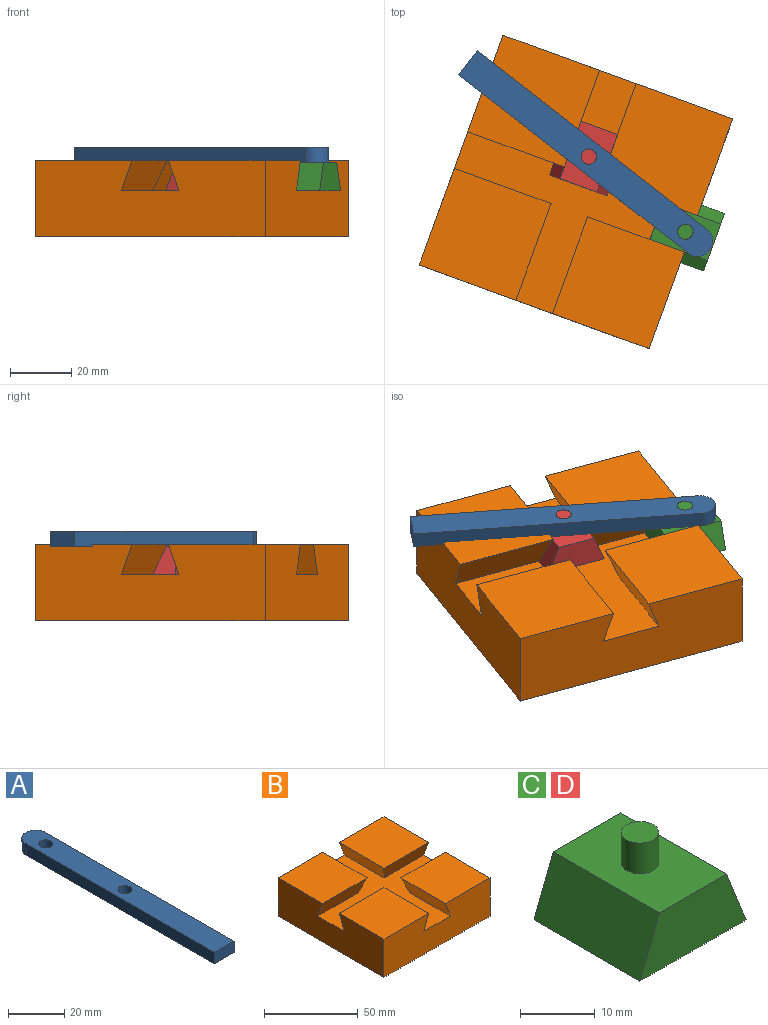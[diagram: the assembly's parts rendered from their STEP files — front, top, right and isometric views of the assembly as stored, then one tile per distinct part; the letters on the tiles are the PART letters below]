
ASSEMBLY  parts=4 mates=4
PART A: 8 faces, bbox 10x100x5 mm
  f0: plane 95x5mm, normal (-1,0,0), area 475mm2, adj f1,f5,f6,f7
  f1: plane 10x5mm, normal (0,-1,0), area 50mm2, adj f0,f2,f5,f6
  f2: plane 95x5mm, normal (1,0,0), area 475mm2, adj f1,f5,f6,f7
  f3: cylinder r=2.5mm len=5mm, axis (0,0,-1), area 78.5mm2, adj f5,f6
  f4: cylinder r=2.5mm len=5mm, axis (0,0,-1), area 78.5mm2, adj f5,f6
  f5: plane 100x10mm, normal (0,0,1), area 950mm2, adj f0,f1,f2,f3,f4,f7
  f6: plane 100x10mm, normal (0,0,-1), area 950mm2, adj f0,f1,f2,f3,f4,f7
  f7: cylinder r=5mm len=10mm, axis (0,0,-1), area 78.5mm2, adj f0,f2,f5,f6
PART B: 18 faces, bbox 80x80x25 mm
  f0: plane 33.64x33.64mm, normal (0,0,1), area 1131.6mm2, adj f5,f7,f12,f17
  f1: plane 33.64x33.64mm, normal (0,0,1), area 1131.6mm2, adj f9,f11,f12,f15
  f2: plane 33.64x10mm, normal (0.94,0,-0.34), area 338.6mm2, adj f4,f6,f13,f16
  f3: plane 33.64x10mm, normal (-0.94,0,-0.34), area 338.6mm2, adj f4,f10,f13,f14
  f4: plane 80x80mm, normal (0,0,1), area 2800mm2, adj f2,f3,f5,f7,f9,f11,f12,f13
  f5: plane 33.64x10mm, normal (0.94,0,-0.34), area 338.6mm2, adj f0,f4,f12,f17
  f6: plane 33.64x33.64mm, normal (0,0,1), area 1131.6mm2, adj f2,f7,f13,f16
  f7: plane 80x25mm, normal (-1,0,0), area 1836.4mm2, adj f0,f4,f6,f8,f12,f13,f16,f17
  f8: plane 80x80mm, normal (0,0,-1), area 6400mm2, adj f7,f9,f12,f13
  f9: plane 80x25mm, normal (1,0,0), area 1836.4mm2, adj f1,f4,f8,f10,f12,f13,f14,f15
  f10: plane 33.64x33.64mm, normal (0,0,1), area 1131.6mm2, adj f3,f9,f13,f14
  f11: plane 33.64x10mm, normal (-0.94,0,-0.34), area 338.6mm2, adj f1,f4,f12,f15
  f12: plane 80x25mm, normal (0,-1,0), area 1836.4mm2, adj f0,f1,f4,f5,f7,f8,f9,f11
  f13: plane 80x25mm, normal (0,1,0), area 1836.4mm2, adj f2,f3,f4,f6,f7,f8,f9,f10
  f14: plane 33.64x10mm, normal (0,-0.94,-0.34), area 338.6mm2, adj f3,f4,f9,f10
  f15: plane 33.64x10mm, normal (0,0.94,-0.34), area 338.6mm2, adj f1,f4,f9,f11
  f16: plane 33.64x10mm, normal (0,-0.94,-0.34), area 338.6mm2, adj f2,f4,f6,f7
  f17: plane 33.64x10mm, normal (0,0.94,-0.34), area 338.6mm2, adj f0,f4,f5,f7
PART C: 8 faces, bbox 20x20x14.3 mm
  f0: plane 20x20mm, normal (0,0,-1), area 400mm2, adj f1,f3,f4,f5
  f1: plane 20x9.31mm, normal (0.93,0,0.36), area 200mm2, adj f0,f2,f4,f5
  f2: plane 20x12.72mm, normal (0,0,1), area 234.8mm2, adj f1,f3,f4,f5,f6
  f3: plane 20x9.31mm, normal (-0.93,0,0.36), area 200mm2, adj f0,f2,f4,f5
  f4: plane 20x9.31mm, normal (0,-1,0), area 152.4mm2, adj f0,f1,f2,f3
  f5: plane 20x9.31mm, normal (0,1,0), area 152.4mm2, adj f0,f1,f2,f3
  f6: cylinder r=2.5mm len=5mm, axis (0,0,-1), area 78.5mm2, adj f2,f7
  f7: plane 5x5mm, normal (0,0,1), area 19.6mm2, adj f6
PART D: same geometry as C
PLACE A rot(axis=(0,0,-1),127.9deg) t=(-10.06,-49.62,4.2)mm
PLACE B rot(axis=(0,0,-1),20deg) t=(84.08,-75.79,-17.38)mm
PLACE C rot(axis=(0,0,-1),110deg) t=(67.3,-112.25,4.2)mm
PLACE D rot(axis=(0,0,-1),20deg) t=(29.76,-74.87,4.2)mm
MATE slider C.f5 <-> B.f9  axis (0.94,-0.34,0) through (67.3,-112.25,-5.12)mm
MATE revolute D.f6 <-> A.f3  axis (0,0,1) through (26.34,-84.27,9.2)mm
MATE revolute C.f6 <-> A.f4  axis (0,0,1) through (57.91,-108.83,9.2)mm
MATE slider D.f5 <-> B.f13  axis (0.34,0.94,0) through (29.76,-74.87,-5.12)mm
